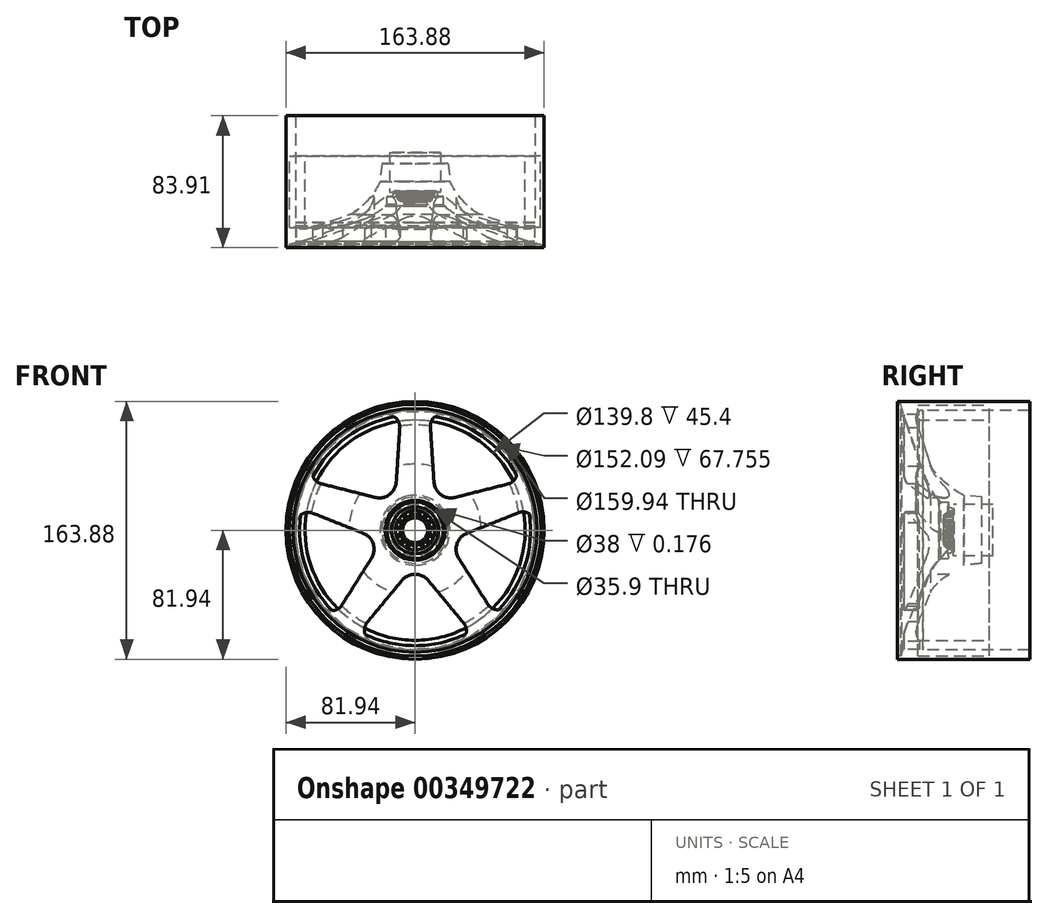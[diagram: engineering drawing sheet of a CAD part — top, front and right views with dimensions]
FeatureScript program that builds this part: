
annotation { "Feature Type Name" : "Feature", "Feature Type Description" : "" }
export const myFeature = defineFeature(function(context is Context, id is Id, definition is map)
    precondition{}
    {
        {
            var Q0;
            Q0=qCreatedBy(makeId("Right.planeOp"),FACE);
            var sketch = newSketch(context, id + "F0", { "sketchPlane" : qUnion([Q0])});
            skLineSegment(sketch, "E0", {"start": v(-89.02, 0) * mm, "end": v(102.14, 0) * mm, "construction": true});
            skLineSegment(sketch, "E1", {"start": v(-1.4, 77.44) * mm, "end": v(10.88, 41.26) * mm});
            skFitSpline(sketch, "E2", {"points": [v(10.88, 41.26) * mm, v(32, 13.4) * mm], "startDerivative": vector(21.53, -61.6) * mm, "endDerivative": vector(25.97, -7.96) * mm});
            skLineSegment(sketch, "E3", {"start": v(32, 13.4) * mm, "end": v(32, 0) * mm});
            skLineSegment(sketch, "E4", {"start": v(32, 0) * mm, "end": v(49.58, 0) * mm});
            skLineSegment(sketch, "E5", {"start": v(49.58, 0) * mm, "end": v(49.58, 21) * mm});
            skLineSegment(sketch, "E6", {"start": v(49.58, 21) * mm, "end": v(38.2, 22.22) * mm});
            skFitSpline(sketch, "E7", {"points": [v(38.2, 22.22) * mm, v(16.97, 42.03) * mm], "startDerivative": vector(-14.65, 4.88) * mm, "endDerivative": vector(-6.21, 22.63) * mm});
            skLineSegment(sketch, "E8", {"start": v(16.97, 42.03) * mm, "end": v(8.9, 66.85) * mm});
            skFitSpline(sketch, "E9", {"points": [v(8.9, 66.85) * mm, v(12.15, 76.05) * mm], "startDerivative": vector(-9.2, 26.3) * mm, "endDerivative": vector(7.1, -0.44) * mm});
            skLineSegment(sketch, "E10", {"start": v(12.15, 76.05) * mm, "end": v(79.9, 76.05) * mm});
            skLineSegment(sketch, "E11", {"start": v(79.9, 76.05) * mm, "end": v(79.9, 81.94) * mm});
            skLineSegment(sketch, "E12", {"start": v(79.9, 81.94) * mm, "end": v(-4.01, 81.94) * mm});
            skLineSegment(sketch, "E13", {"start": v(-4.01, 81.94) * mm, "end": v(-3.68, 79.97) * mm});
            skLineSegment(sketch, "E14", {"start": v(-3.68, 79.97) * mm, "end": v(-1.9, 79.97) * mm});
            skLineSegment(sketch, "E15", {"start": v(-1.9, 79.97) * mm, "end": v(-1.37, 77.44) * mm});
            skLineSegment(sketch, "E16", {"start": v(-1.4, 77.44) * mm, "end": v(-1.37, 77.44) * mm});
            skSolve(sketch);
        }
        {
            var Q0;
            Q0 = qSketchRegion(id + "F0", true);
            var Q1;
            Q1=sQuery(id+"F0.wireOp",EDGE,"E0");
            revolve(context, id + "F1", {"entities" : qUnion([Q0]), "axis" : qUnion([Q1]), "revolveType" : RevolveType.FULL});
        }
        {
            var Q0;
            Q0=qCreatedBy(makeId("Front.planeOp"),FACE);
            var sketch = newSketch(context, id + "F2", { "sketchPlane" : qUnion([Q0])});
            skLineSegment(sketch, "E17", {"start": v(-9.75, 64.99) * mm, "end": v(-11.97, 30.73) * mm});
            skLineSegment(sketch, "E18", {"start": v(0, 99.35) * mm, "end": v(0, -96.83) * mm, "construction": true});
            skLineSegment(sketch, "E19", {"start": v(-69.73, 95.98) * mm, "end": v(0, 0) * mm, "construction": true});
            skLineSegment(sketch, "E20.MirrorCS", {"start": v(-58.8, 29.36) * mm, "end": v(-25.53, 20.88) * mm});
            skArc(sketch, "E21", {"start": v(-64.04, 40.61) * mm, "mid": v(-44.57, 61.35) * mm, "end": v(-18.84, 73.45) * mm});
            skArc(sketch, "E22", {"start": v(-11.97, 30.73) * mm, "mid": v(-16.44, 22.62) * mm, "end": v(-25.53, 20.88) * mm});
            skArc(sketch, "E23", {"start": v(-9.75, 64.99) * mm, "mid": v(-12.29, 71.37) * mm, "end": v(-18.84, 73.45) * mm});
            skArc(sketch, "E24", {"start": v(-64.04, 40.61) * mm, "mid": v(-64.5, 33.55) * mm, "end": v(-58.8, 29.36) * mm});
            skLineSegment(sketch, "E25.1.0", {"start": v(-64.82, 10.8) * mm, "end": v(-32.93, -1.89) * mm});
            skArc(sketch, "E25.1.1", {"start": v(-64.82, 10.8) * mm, "mid": v(-71.68, 10.37) * mm, "end": v(-75.68, 4.78) * mm});
            skArc(sketch, "E25.1.2", {"start": v(-58.42, -48.35) * mm, "mid": v(-72.12, -23.43) * mm, "end": v(-75.68, 4.78) * mm});
            skArc(sketch, "E25.1.3", {"start": v(-58.42, -48.35) * mm, "mid": v(-51.84, -50.97) * mm, "end": v(-46.09, -46.84) * mm});
            skLineSegment(sketch, "E25.1.4", {"start": v(-46.09, -46.84) * mm, "end": v(-27.75, -17.83) * mm});
            skArc(sketch, "E25.1.5", {"start": v(-32.93, -1.89) * mm, "mid": v(-26.6, -8.64) * mm, "end": v(-27.75, -17.83) * mm});
            skLineSegment(sketch, "E25.2.0", {"start": v(-30.31, -58.3) * mm, "end": v(-8.38, -31.9) * mm});
            skArc(sketch, "E25.2.1", {"start": v(-30.31, -58.3) * mm, "mid": v(-32.01, -64.97) * mm, "end": v(-27.93, -70.5) * mm});
            skArc(sketch, "E25.2.2", {"start": v(27.93, -70.5) * mm, "mid": v(0, -75.83) * mm, "end": v(-27.93, -70.5) * mm});
            skArc(sketch, "E25.2.3", {"start": v(27.93, -70.5) * mm, "mid": v(32.46, -65.05) * mm, "end": v(30.31, -58.3) * mm});
            skLineSegment(sketch, "E25.2.4", {"start": v(30.31, -58.3) * mm, "end": v(8.38, -31.9) * mm});
            skArc(sketch, "E25.2.5", {"start": v(-8.38, -31.9) * mm, "mid": v(0, -27.96) * mm, "end": v(8.38, -31.9) * mm});
            skLineSegment(sketch, "E25.3.0", {"start": v(46.09, -46.84) * mm, "end": v(27.75, -17.83) * mm});
            skArc(sketch, "E25.3.1", {"start": v(46.09, -46.84) * mm, "mid": v(51.9, -50.52) * mm, "end": v(58.42, -48.35) * mm});
            skArc(sketch, "E25.3.2", {"start": v(75.68, 4.78) * mm, "mid": v(72.12, -23.43) * mm, "end": v(58.42, -48.35) * mm});
            skArc(sketch, "E25.3.3", {"start": v(75.68, 4.78) * mm, "mid": v(71.9, 10.76) * mm, "end": v(64.82, 10.8) * mm});
            skLineSegment(sketch, "E25.3.4", {"start": v(64.82, 10.8) * mm, "end": v(32.93, -1.89) * mm});
            skArc(sketch, "E25.3.5", {"start": v(27.75, -17.83) * mm, "mid": v(26.6, -8.64) * mm, "end": v(32.93, -1.89) * mm});
            skLineSegment(sketch, "E25.4.0", {"start": v(58.8, 29.36) * mm, "end": v(25.53, 20.88) * mm});
            skArc(sketch, "E25.4.1", {"start": v(58.8, 29.36) * mm, "mid": v(64.08, 33.74) * mm, "end": v(64.04, 40.61) * mm});
            skArc(sketch, "E25.4.2", {"start": v(18.84, 73.45) * mm, "mid": v(44.57, 61.35) * mm, "end": v(64.04, 40.61) * mm});
            skArc(sketch, "E25.4.3", {"start": v(18.84, 73.45) * mm, "mid": v(11.98, 71.7) * mm, "end": v(9.75, 64.99) * mm});
            skLineSegment(sketch, "E25.4.4", {"start": v(9.75, 64.99) * mm, "end": v(11.97, 30.73) * mm});
            skArc(sketch, "E25.4.5", {"start": v(25.53, 20.88) * mm, "mid": v(16.44, 22.62) * mm, "end": v(11.97, 30.73) * mm});
            skSolve(sketch);
        }
        {
            var Q0;
            Q0=makeQuery(id+"F2.imprint","IMPRINT",FACE,{"disambiguationData":[TD([[makeQuery(id+"F2.imprint","IMPRINT",EDGE,{"derivedFrom":sQuery(id+"F2.wireOp",EDGE,"E17")}),-1.0]])]});
            var Q1;
            Q1=makeQuery(id+"F2.imprint","IMPRINT",FACE,{"disambiguationData":[TD([[makeQuery(id+"F2.imprint","IMPRINT",EDGE,{"derivedFrom":sQuery(id+"F2.wireOp",EDGE,"E25.4.0")}),-1.0]])]});
            var Q2;
            Q2=makeQuery(id+"F2.imprint","IMPRINT",FACE,{"disambiguationData":[TD([[makeQuery(id+"F2.imprint","IMPRINT",EDGE,{"derivedFrom":sQuery(id+"F2.wireOp",EDGE,"E25.3.0")}),-1.0]])]});
            var Q3;
            Q3=makeQuery(id+"F2.imprint","IMPRINT",FACE,{"disambiguationData":[TD([[makeQuery(id+"F2.imprint","IMPRINT",EDGE,{"derivedFrom":sQuery(id+"F2.wireOp",EDGE,"E25.2.0")}),-1.0]])]});
            var Q4;
            Q4=makeQuery(id+"F2.imprint","IMPRINT",FACE,{"disambiguationData":[TD([[makeQuery(id+"F2.imprint","IMPRINT",EDGE,{"derivedFrom":sQuery(id+"F2.wireOp",EDGE,"E25.1.0")}),-1.0]])]});
            extrude(context, id + "F3", {"entities" : qUnion([Q0, Q1, Q2, Q3, Q4]), "operationType" : NewBodyOperationType.REMOVE, "endBound" : BoundingType.THROUGH_ALL, "oppositeDirection" : true, "depth" : 87.88 * mm});
        }
        {
            var Q0;
            Q0=qCreatedBy(makeId("Front.planeOp"),FACE);
            cPlane(context, id + "F4", {"entities" : qUnion([Q0]), "cplaneType" : CPlaneType.OFFSET, "offset" : 31.5 * mm, "oppositeDirection" : true, "width" : 150 * mm, "height" : 150 * mm});
        }
        {
            var Q0;
            Q0=qCreatedBy(id+"F4.planeOp",FACE);
            var sketch = newSketch(context, id + "F5", { "sketchPlane" : qUnion([Q0])});
            skCircle(sketch, "E26", {"center": v(0, 0) * mm, "radius": 16.28 * mm});
            skSolve(sketch);
        }
        {
            var Q0;
            Q0 = qSketchRegion(id + "F5", true);
            extrude(context, id + "F6", {"entities" : qUnion([Q0]), "oppositeDirection" : true, "depth" : 25 * mm});
        }
        {
            var Q0;
            Q0=qCreatedBy(id+"F4.planeOp",FACE);
            var sketch = newSketch(context, id + "F7", { "sketchPlane" : qUnion([Q0])});
            skCircle(sketch, "E27", {"center": v(0, 0) * mm, "radius": 12.5 * mm});
            skSolve(sketch);
        }
        {
            var Q0;
            Q0 = qSketchRegion(id + "F7", true);
            extrude(context, id + "F8", {"entities" : qUnion([Q0]), "depth" : 1.5 * mm});
        }
        {
            var Q0;
            Q0=qCreatedBy(id+"F4.planeOp",FACE);
            var sketch = newSketch(context, id + "F9", { "sketchPlane" : qUnion([Q0])});
            skLineSegment(sketch, "E28", {"start": v(0, 0) * mm, "end": v(0, 19.42) * mm, "construction": true});
            skLineSegment(sketch, "E29", {"start": v(-17.58, 0) * mm, "end": v(17.07, 0) * mm, "construction": true});
            skLineSegment(sketch, "E30", {"start": v(0, 0) * mm, "end": v(0, -17.5) * mm, "construction": true});
            skLineSegment(sketch, "E31", {"start": v(-1.31, -9.3) * mm, "end": v(-0.63, -11.05) * mm});
            skLineSegment(sketch, "E32.MirrorCS", {"start": v(1.31, -9.3) * mm, "end": v(0.63, -11.05) * mm});
            skArc(sketch, "E33", {"start": v(0.63, -11.05) * mm, "mid": v(0, -11.07) * mm, "end": v(-0.63, -11.05) * mm});
            skLineSegment(sketch, "E34", {"start": v(0, 0) * mm, "end": v(3.1, -14.56) * mm, "construction": true});
            skArc(sketch, "E35", {"start": v(1.31, -9.3) * mm, "mid": v(1.63, -9.25) * mm, "end": v(1.95, -9.19) * mm});
            skArc(sketch, "E36.MirrorCS", {"start": v(-1.31, -9.3) * mm, "mid": v(-1.63, -9.25) * mm, "end": v(-1.95, -9.19) * mm});
            skArc(sketch, "E37.1.0", {"start": v(2.58, -9.03) * mm, "mid": v(2.27, -9.12) * mm, "end": v(1.95, -9.19) * mm});
            skLineSegment(sketch, "E37.1.1", {"start": v(2.58, -9.03) * mm, "end": v(3.92, -10.35) * mm});
            skArc(sketch, "E37.1.2", {"start": v(5.07, -9.84) * mm, "mid": v(4.5, -10.11) * mm, "end": v(3.92, -10.35) * mm});
            skLineSegment(sketch, "E37.1.3", {"start": v(4.98, -7.96) * mm, "end": v(5.07, -9.84) * mm});
            skArc(sketch, "E37.1.4", {"start": v(4.98, -7.96) * mm, "mid": v(5.26, -7.79) * mm, "end": v(5.52, -7.6) * mm});
            skArc(sketch, "E37.2.0", {"start": v(6.03, -7.2) * mm, "mid": v(5.78, -7.4) * mm, "end": v(5.52, -7.6) * mm});
            skLineSegment(sketch, "E37.2.1", {"start": v(6.03, -7.2) * mm, "end": v(7.8, -7.87) * mm});
            skArc(sketch, "E37.2.2", {"start": v(8.64, -6.93) * mm, "mid": v(8.23, -7.4) * mm, "end": v(7.8, -7.87) * mm});
            skLineSegment(sketch, "E37.2.3", {"start": v(7.8, -5.25) * mm, "end": v(8.64, -6.93) * mm});
            skArc(sketch, "E37.2.4", {"start": v(7.8, -5.25) * mm, "mid": v(7.97, -4.98) * mm, "end": v(8.14, -4.7) * mm});
            skArc(sketch, "E37.3.0", {"start": v(8.44, -4.12) * mm, "mid": v(8.3, -4.41) * mm, "end": v(8.14, -4.7) * mm});
            skLineSegment(sketch, "E37.3.1", {"start": v(8.44, -4.12) * mm, "end": v(10.32, -4.02) * mm});
            skArc(sketch, "E37.3.2", {"start": v(10.7, -2.81) * mm, "mid": v(10.53, -3.42) * mm, "end": v(10.32, -4.02) * mm});
            skLineSegment(sketch, "E37.3.3", {"start": v(9.25, -1.63) * mm, "end": v(10.7, -2.81) * mm});
            skArc(sketch, "E37.3.4", {"start": v(9.25, -1.63) * mm, "mid": v(9.3, -1.3) * mm, "end": v(9.34, -0.98) * mm});
            skArc(sketch, "E37.4.0", {"start": v(9.39, -0.33) * mm, "mid": v(9.37, -0.66) * mm, "end": v(9.34, -0.98) * mm});
            skLineSegment(sketch, "E37.4.1", {"start": v(9.39, -0.33) * mm, "end": v(11.06, 0.53) * mm});
            skArc(sketch, "E37.4.2", {"start": v(10.93, 1.78) * mm, "mid": v(11.01, 1.16) * mm, "end": v(11.06, 0.53) * mm});
            skLineSegment(sketch, "E37.4.3", {"start": v(9.11, 2.28) * mm, "end": v(10.93, 1.78) * mm});
            skArc(sketch, "E37.4.4", {"start": v(9.11, 2.28) * mm, "mid": v(9.03, 2.6) * mm, "end": v(8.94, 2.9) * mm});
            skArc(sketch, "E37.5.0", {"start": v(8.71, 3.51) * mm, "mid": v(8.83, 3.21) * mm, "end": v(8.94, 2.9) * mm});
            skLineSegment(sketch, "E37.5.1", {"start": v(8.71, 3.51) * mm, "end": v(9.89, 4.98) * mm});
            skArc(sketch, "E37.5.2", {"start": v(9.26, 6.07) * mm, "mid": v(9.59, 5.54) * mm, "end": v(9.89, 4.98) * mm});
            skLineSegment(sketch, "E37.5.3", {"start": v(7.4, 5.79) * mm, "end": v(9.26, 6.07) * mm});
            skArc(sketch, "E37.5.4", {"start": v(7.4, 5.79) * mm, "mid": v(7.2, 6.04) * mm, "end": v(6.98, 6.29) * mm});
            skArc(sketch, "E37.6.0", {"start": v(6.53, 6.75) * mm, "mid": v(6.76, 6.52) * mm, "end": v(6.98, 6.29) * mm});
            skLineSegment(sketch, "E37.6.1", {"start": v(6.53, 6.75) * mm, "end": v(7, 8.57) * mm});
            skArc(sketch, "E37.6.2", {"start": v(5.99, 9.31) * mm, "mid": v(6.5, 8.96) * mm, "end": v(7, 8.57) * mm});
            skLineSegment(sketch, "E37.6.3", {"start": v(4.4, 8.3) * mm, "end": v(5.99, 9.31) * mm});
            skArc(sketch, "E37.6.4", {"start": v(4.4, 8.3) * mm, "mid": v(4.12, 8.45) * mm, "end": v(3.82, 8.58) * mm});
            skArc(sketch, "E37.7.0", {"start": v(3.22, 8.83) * mm, "mid": v(3.52, 8.7) * mm, "end": v(3.82, 8.58) * mm});
            skLineSegment(sketch, "E37.7.1", {"start": v(3.22, 8.83) * mm, "end": v(2.92, 10.68) * mm});
            skArc(sketch, "E37.7.2", {"start": v(1.68, 10.94) * mm, "mid": v(2.3, 10.83) * mm, "end": v(2.92, 10.68) * mm});
            skLineSegment(sketch, "E37.7.3", {"start": v(0.65, 9.37) * mm, "end": v(1.68, 10.94) * mm});
            skArc(sketch, "E37.7.4", {"start": v(0.65, 9.37) * mm, "mid": v(0.32, 9.39) * mm, "end": v(0, 9.4) * mm});
            skArc(sketch, "E37.8.0", {"start": v(-0.65, 9.37) * mm, "mid": v(-0.32, 9.39) * mm, "end": v(0, 9.4) * mm});
            skLineSegment(sketch, "E37.8.1", {"start": v(-0.65, 9.37) * mm, "end": v(-1.68, 10.94) * mm});
            skArc(sketch, "E37.8.2", {"start": v(-2.92, 10.68) * mm, "mid": v(-2.3, 10.83) * mm, "end": v(-1.68, 10.94) * mm});
            skLineSegment(sketch, "E37.8.3", {"start": v(-3.22, 8.83) * mm, "end": v(-2.92, 10.68) * mm});
            skArc(sketch, "E37.8.4", {"start": v(-3.22, 8.83) * mm, "mid": v(-3.52, 8.7) * mm, "end": v(-3.82, 8.58) * mm});
            skArc(sketch, "E37.9.0", {"start": v(-4.4, 8.3) * mm, "mid": v(-4.12, 8.45) * mm, "end": v(-3.82, 8.58) * mm});
            skLineSegment(sketch, "E37.9.1", {"start": v(-4.4, 8.3) * mm, "end": v(-5.99, 9.31) * mm});
            skArc(sketch, "E37.9.2", {"start": v(-7, 8.57) * mm, "mid": v(-6.5, 8.96) * mm, "end": v(-5.99, 9.31) * mm});
            skLineSegment(sketch, "E37.9.3", {"start": v(-6.53, 6.75) * mm, "end": v(-7, 8.57) * mm});
            skArc(sketch, "E37.9.4", {"start": v(-6.53, 6.75) * mm, "mid": v(-6.76, 6.52) * mm, "end": v(-6.98, 6.29) * mm});
            skArc(sketch, "E37.10.0", {"start": v(-7.4, 5.79) * mm, "mid": v(-7.2, 6.04) * mm, "end": v(-6.98, 6.29) * mm});
            skLineSegment(sketch, "E37.10.1", {"start": v(-7.4, 5.79) * mm, "end": v(-9.26, 6.07) * mm});
            skArc(sketch, "E37.10.2", {"start": v(-9.89, 4.98) * mm, "mid": v(-9.59, 5.54) * mm, "end": v(-9.26, 6.07) * mm});
            skLineSegment(sketch, "E37.10.3", {"start": v(-8.71, 3.51) * mm, "end": v(-9.89, 4.98) * mm});
            skArc(sketch, "E37.10.4", {"start": v(-8.71, 3.51) * mm, "mid": v(-8.83, 3.21) * mm, "end": v(-8.94, 2.9) * mm});
            skArc(sketch, "E37.11.0", {"start": v(-9.11, 2.28) * mm, "mid": v(-9.03, 2.6) * mm, "end": v(-8.94, 2.9) * mm});
            skLineSegment(sketch, "E37.11.1", {"start": v(-9.11, 2.28) * mm, "end": v(-10.93, 1.78) * mm});
            skArc(sketch, "E37.11.2", {"start": v(-11.06, 0.53) * mm, "mid": v(-11.01, 1.16) * mm, "end": v(-10.93, 1.78) * mm});
            skLineSegment(sketch, "E37.11.3", {"start": v(-9.39, -0.33) * mm, "end": v(-11.06, 0.53) * mm});
            skArc(sketch, "E37.11.4", {"start": v(-9.39, -0.33) * mm, "mid": v(-9.37, -0.66) * mm, "end": v(-9.34, -0.98) * mm});
            skArc(sketch, "E37.12.0", {"start": v(-9.25, -1.63) * mm, "mid": v(-9.3, -1.3) * mm, "end": v(-9.34, -0.98) * mm});
            skLineSegment(sketch, "E37.12.1", {"start": v(-9.25, -1.63) * mm, "end": v(-10.7, -2.81) * mm});
            skArc(sketch, "E37.12.2", {"start": v(-10.32, -4.02) * mm, "mid": v(-10.53, -3.42) * mm, "end": v(-10.7, -2.81) * mm});
            skLineSegment(sketch, "E37.12.3", {"start": v(-8.44, -4.12) * mm, "end": v(-10.32, -4.02) * mm});
            skArc(sketch, "E37.12.4", {"start": v(-8.44, -4.12) * mm, "mid": v(-8.3, -4.41) * mm, "end": v(-8.14, -4.7) * mm});
            skArc(sketch, "E37.13.0", {"start": v(-7.8, -5.25) * mm, "mid": v(-7.97, -4.98) * mm, "end": v(-8.14, -4.7) * mm});
            skLineSegment(sketch, "E37.13.1", {"start": v(-7.8, -5.25) * mm, "end": v(-8.64, -6.93) * mm});
            skArc(sketch, "E37.13.2", {"start": v(-7.8, -7.87) * mm, "mid": v(-8.23, -7.4) * mm, "end": v(-8.64, -6.93) * mm});
            skLineSegment(sketch, "E37.13.3", {"start": v(-6.03, -7.2) * mm, "end": v(-7.8, -7.87) * mm});
            skArc(sketch, "E37.13.4", {"start": v(-6.03, -7.2) * mm, "mid": v(-5.78, -7.4) * mm, "end": v(-5.52, -7.6) * mm});
            skArc(sketch, "E37.14.0", {"start": v(-4.98, -7.96) * mm, "mid": v(-5.26, -7.79) * mm, "end": v(-5.52, -7.6) * mm});
            skLineSegment(sketch, "E37.14.1", {"start": v(-4.98, -7.96) * mm, "end": v(-5.07, -9.84) * mm});
            skArc(sketch, "E37.14.2", {"start": v(-3.92, -10.35) * mm, "mid": v(-4.5, -10.11) * mm, "end": v(-5.07, -9.84) * mm});
            skLineSegment(sketch, "E37.14.3", {"start": v(-2.58, -9.03) * mm, "end": v(-3.92, -10.35) * mm});
            skArc(sketch, "E37.14.4", {"start": v(-2.58, -9.03) * mm, "mid": v(-2.27, -9.12) * mm, "end": v(-1.95, -9.19) * mm});
            skSolve(sketch);
        }
        {
            var Q0;
            Q0 = qSketchRegion(id + "F9", true);
            extrude(context, id + "F10", {"entities" : qUnion([Q0]), "depth" : 6 * mm});
        }
        {
            var Q0;
            Q0=qCreatedBy(makeId("Right.planeOp"),FACE);
            var sketch = newSketch(context, id + "F11", { "sketchPlane" : qUnion([Q0])});
            skLineSegment(sketch, "E38", {"start": v(27.73, 11.93) * mm, "end": v(17.1, 0.98) * mm});
            skLineSegment(sketch, "E39", {"start": v(17.1, 0.98) * mm, "end": v(17.1, 17.95) * mm});
            skLineSegment(sketch, "E40", {"start": v(17.1, 17.95) * mm, "end": v(28.4, 17.95) * mm});
            skLineSegment(sketch, "E41", {"start": v(28.4, 17.95) * mm, "end": v(27.73, 11.93) * mm});
            skLineSegment(sketch, "E42", {"start": v(0, 0) * mm, "end": v(38.16, 0) * mm, "construction": true});
            skSolve(sketch);
        }
        {
            var Q0;
            Q0=makeQuery(id+"F11.imprint","IMPRINT",FACE,{"disambiguationData":[TD([[makeQuery(id+"F11.imprint","IMPRINT",EDGE,{"derivedFrom":sQuery(id+"F11.wireOp",EDGE,"E38")}),-1.0]])]});
            var Q1;
            Q1=sQuery(id+"F11.wireOp",EDGE,"E42");
            revolve(context, id + "F12", {"operationType" : NewBodyOperationType.REMOVE, "entities" : qUnion([Q0]), "axis" : qUnion([Q1]), "revolveType" : RevolveType.FULL, "oppositeDirection" : true});
        }
        {
            var Q0;
            Q0=makeQuery(id+"F10.opExtrude","CAP_FACE",FACE,{"disambiguationData":[OSD([sQuery(id+"F9.wireOp",EDGE,"E31"),sQuery(id+"F9.wireOp",EDGE,"E32.MirrorCS"),sQuery(id+"F9.wireOp",EDGE,"E33"),sQuery(id+"F9.wireOp",EDGE,"E35"),sQuery(id+"F9.wireOp",EDGE,"E36.MirrorCS"),sQuery(id+"F9.wireOp",EDGE,"E37.1.0"),sQuery(id+"F9.wireOp",EDGE,"E37.1.1"),sQuery(id+"F9.wireOp",EDGE,"E37.1.2"),sQuery(id+"F9.wireOp",EDGE,"E37.1.3"),sQuery(id+"F9.wireOp",EDGE,"E37.1.4"),sQuery(id+"F9.wireOp",EDGE,"E37.2.0"),sQuery(id+"F9.wireOp",EDGE,"E37.2.1"),sQuery(id+"F9.wireOp",EDGE,"E37.2.2"),sQuery(id+"F9.wireOp",EDGE,"E37.2.3"),sQuery(id+"F9.wireOp",EDGE,"E37.2.4"),sQuery(id+"F9.wireOp",EDGE,"E37.3.0"),sQuery(id+"F9.wireOp",EDGE,"E37.3.1"),sQuery(id+"F9.wireOp",EDGE,"E37.3.2"),sQuery(id+"F9.wireOp",EDGE,"E37.3.3"),sQuery(id+"F9.wireOp",EDGE,"E37.3.4"),sQuery(id+"F9.wireOp",EDGE,"E37.4.0"),sQuery(id+"F9.wireOp",EDGE,"E37.4.1"),sQuery(id+"F9.wireOp",EDGE,"E37.4.2"),sQuery(id+"F9.wireOp",EDGE,"E37.4.3"),sQuery(id+"F9.wireOp",EDGE,"E37.4.4"),sQuery(id+"F9.wireOp",EDGE,"E37.5.0"),sQuery(id+"F9.wireOp",EDGE,"E37.5.1"),sQuery(id+"F9.wireOp",EDGE,"E37.5.2"),sQuery(id+"F9.wireOp",EDGE,"E37.5.3"),sQuery(id+"F9.wireOp",EDGE,"E37.5.4"),sQuery(id+"F9.wireOp",EDGE,"E37.6.0"),sQuery(id+"F9.wireOp",EDGE,"E37.6.1"),sQuery(id+"F9.wireOp",EDGE,"E37.6.2"),sQuery(id+"F9.wireOp",EDGE,"E37.6.3"),sQuery(id+"F9.wireOp",EDGE,"E37.6.4"),sQuery(id+"F9.wireOp",EDGE,"E37.7.0"),sQuery(id+"F9.wireOp",EDGE,"E37.7.1"),sQuery(id+"F9.wireOp",EDGE,"E37.7.2"),sQuery(id+"F9.wireOp",EDGE,"E37.7.3"),sQuery(id+"F9.wireOp",EDGE,"E37.7.4"),sQuery(id+"F9.wireOp",EDGE,"E37.8.0"),sQuery(id+"F9.wireOp",EDGE,"E37.8.1"),sQuery(id+"F9.wireOp",EDGE,"E37.8.2"),sQuery(id+"F9.wireOp",EDGE,"E37.8.3"),sQuery(id+"F9.wireOp",EDGE,"E37.8.4"),sQuery(id+"F9.wireOp",EDGE,"E37.9.0"),sQuery(id+"F9.wireOp",EDGE,"E37.9.1"),sQuery(id+"F9.wireOp",EDGE,"E37.9.2"),sQuery(id+"F9.wireOp",EDGE,"E37.9.3"),sQuery(id+"F9.wireOp",EDGE,"E37.9.4"),sQuery(id+"F9.wireOp",EDGE,"E37.10.0"),sQuery(id+"F9.wireOp",EDGE,"E37.10.1"),sQuery(id+"F9.wireOp",EDGE,"E37.10.2"),sQuery(id+"F9.wireOp",EDGE,"E37.10.3"),sQuery(id+"F9.wireOp",EDGE,"E37.10.4"),sQuery(id+"F9.wireOp",EDGE,"E37.11.0"),sQuery(id+"F9.wireOp",EDGE,"E37.11.1"),sQuery(id+"F9.wireOp",EDGE,"E37.11.2"),sQuery(id+"F9.wireOp",EDGE,"E37.11.3"),sQuery(id+"F9.wireOp",EDGE,"E37.11.4"),sQuery(id+"F9.wireOp",EDGE,"E37.12.0"),sQuery(id+"F9.wireOp",EDGE,"E37.12.1"),sQuery(id+"F9.wireOp",EDGE,"E37.12.2"),sQuery(id+"F9.wireOp",EDGE,"E37.12.3"),sQuery(id+"F9.wireOp",EDGE,"E37.12.4"),sQuery(id+"F9.wireOp",EDGE,"E37.13.0"),sQuery(id+"F9.wireOp",EDGE,"E37.13.1"),sQuery(id+"F9.wireOp",EDGE,"E37.13.2"),sQuery(id+"F9.wireOp",EDGE,"E37.13.3"),sQuery(id+"F9.wireOp",EDGE,"E37.13.4"),sQuery(id+"F9.wireOp",EDGE,"E37.14.0"),sQuery(id+"F9.wireOp",EDGE,"E37.14.1"),sQuery(id+"F9.wireOp",EDGE,"E37.14.2"),sQuery(id+"F9.wireOp",EDGE,"E37.14.3"),sQuery(id+"F9.wireOp",EDGE,"E37.14.4")])],"isStart":false});
            var sketch = newSketch(context, id + "F13", { "sketchPlane" : qUnion([Q0])});
            skCircle(sketch, "E43", {"center": v(0, 0) * mm, "radius": 7.95 * mm});
            skSolve(sketch);
        }
        {
            var Q0;
            Q0 = qSketchRegion(id + "F13", true);
            extrude(context, id + "F14", {"entities" : qUnion([Q0]), "depth" : .5 * mm});
        }
        {
            var Q0;
            Q0=makeQuery(id+"F14.opExtrude","CAP_EDGE",EDGE,{"disambiguationData":[OSD([sQuery(id+"F13.wireOp",EDGE,"E43")])],"isStart":false});
            fillet(context, id + "F15", {"entities" : qUnion([Q0]), "radius" : .5 * mm, "tangentPropagation" : true, "allowEdgeOverflow" : false});
        }
        {
            var Q0;
            Q0=qCreatedBy(id+"F4.planeOp",FACE);
            var sketch = newSketch(context, id + "F16", { "sketchPlane" : qUnion([Q0])});
            skCircle(sketch, "E44", {"center": v(0, 0) * mm, "radius": 79.68 * mm});
            skCircle(sketch, "E45", {"center": v(0, 0) * mm, "radius": 69.9 * mm});
            skSolve(sketch);
        }
        {
            var Q0;
            Q0 = qSketchRegion(id + "F16", true);
            extrude(context, id + "F17", {"entities" : qUnion([Q0]), "depth" : 45.4 * mm, "symmetric" : true});
        }
        {
            var Q0;
            Q0=qCreatedBy(makeId("Front.planeOp"),FACE);
            var sketch = newSketch(context, id + "F18", { "sketchPlane" : qUnion([Q0])});
            skCircle(sketch, "E46", {"center": v(0, 0) * mm, "radius": 19 * mm});
            skSolve(sketch);
        }
        {
            var Q0;
            Q0 = qSketchRegion(id + "F18", true);
            extrude(context, id + "F19", {"entities" : qUnion([Q0]), "operationType" : NewBodyOperationType.REMOVE, "oppositeDirection" : true, "depth" : 22.5 * mm});
        }
    });
